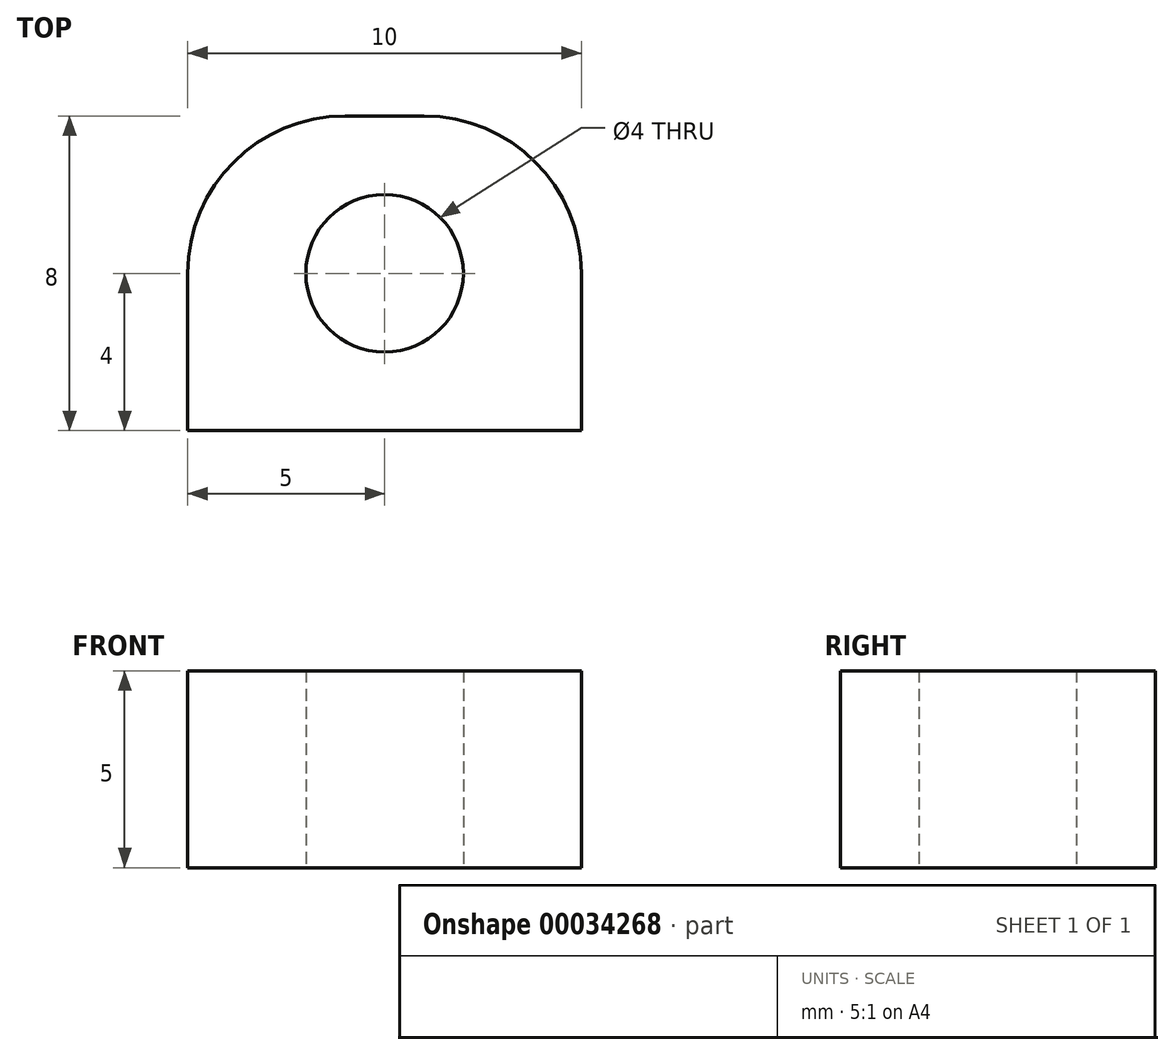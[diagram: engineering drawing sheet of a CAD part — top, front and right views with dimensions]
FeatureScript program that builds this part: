
annotation { "Feature Type Name" : "Feature", "Feature Type Description" : "" }
export const myFeature = defineFeature(function(context is Context, id is Id, definition is map)
    precondition{}
    {
        {
            var Q0;
            Q0=qCreatedBy(makeId("Top.planeOp"),FACE);
            var sketch = newSketch(context, id + "F0", { "sketchPlane" : qUnion([Q0])});
            skLineSegment(sketch, "E0.rect.bottom", {"start": v(5, -4) * mm, "end": v(-5, -4) * mm});
            skLineSegment(sketch, "E0.rect.top", {"start": v(1, 4) * mm, "end": v(-1, 4) * mm});
            skLineSegment(sketch, "E0.rect.left", {"start": v(5, -4) * mm, "end": v(5, 0) * mm});
            skLineSegment(sketch, "E0.rect.right", {"start": v(-5, -4) * mm, "end": v(-5, 0) * mm});
            skPoint(sketch, "E0.rect.middle", {"position": v(0, 0) * mm});
            skCircle(sketch, "E1", {"center": v(0, 0) * mm, "radius": 2 * mm});
            skPoint(sketch, "E2.visualSharp", {"position": v(-5, 4) * mm});
            skArc(sketch, "E2.filletArc", {"start": v(-1, 4) * mm, "mid": v(-3.83, 2.83) * mm, "end": v(-5, 0) * mm});
            skPoint(sketch, "E3.visualSharp", {"position": v(5, 4) * mm});
            skArc(sketch, "E3.filletArc", {"start": v(5, 0) * mm, "mid": v(3.83, 2.83) * mm, "end": v(1, 4) * mm});
            skSolve(sketch);
        }
        {
            var Q0;
            Q0=makeQuery(id+"F0.imprint","IMPRINT",FACE,{"disambiguationData":[TD([[makeQuery(id+"F0.imprint","IMPRINT",EDGE,{"derivedFrom":sQuery(id+"F0.wireOp",EDGE,"E0.rect.bottom")}),-1.0]])]});
            extrude(context, id + "F1", {"entities" : qUnion([Q0]), "depth" : 5 * mm});
        }
    });
